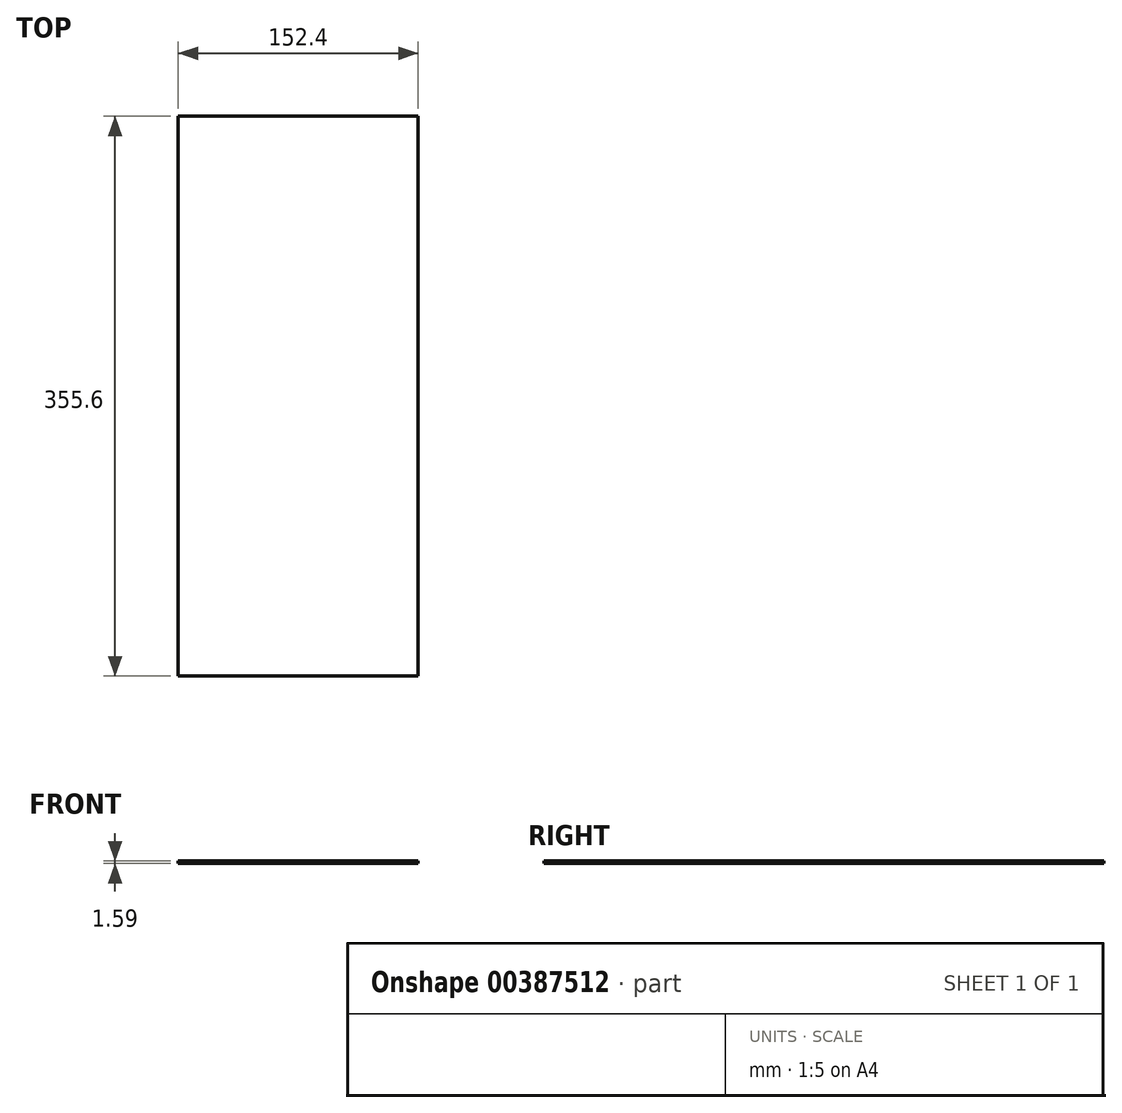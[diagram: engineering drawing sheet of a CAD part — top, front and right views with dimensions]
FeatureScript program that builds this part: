
annotation { "Feature Type Name" : "Feature", "Feature Type Description" : "" }
export const myFeature = defineFeature(function(context is Context, id is Id, definition is map)
    precondition{}
    {
        {
            var Q0;
            Q0=qCreatedBy(makeId("Top.planeOp"),FACE);
            var sketch = newSketch(context, id + "F0", { "sketchPlane" : qUnion([Q0])});
            skLineSegment(sketch, "E0.bottom", {"start": v(0, 0) * mm, "end": v(152.4, 0) * mm});
            skLineSegment(sketch, "E0.top", {"start": v(0, 355.6) * mm, "end": v(152.4, 355.6) * mm});
            skLineSegment(sketch, "E0.left", {"start": v(0, 0) * mm, "end": v(0, 355.6) * mm});
            skLineSegment(sketch, "E0.right", {"start": v(152.4, 0) * mm, "end": v(152.4, 355.6) * mm});
            skSolve(sketch);
        }
        {
            var Q0;
            Q0 = qSketchRegion(id + "F0", true);
            extrude(context, id + "F1", {"entities" : qUnion([Q0]), "depth" : 1.59 * mm});
        }
    });
